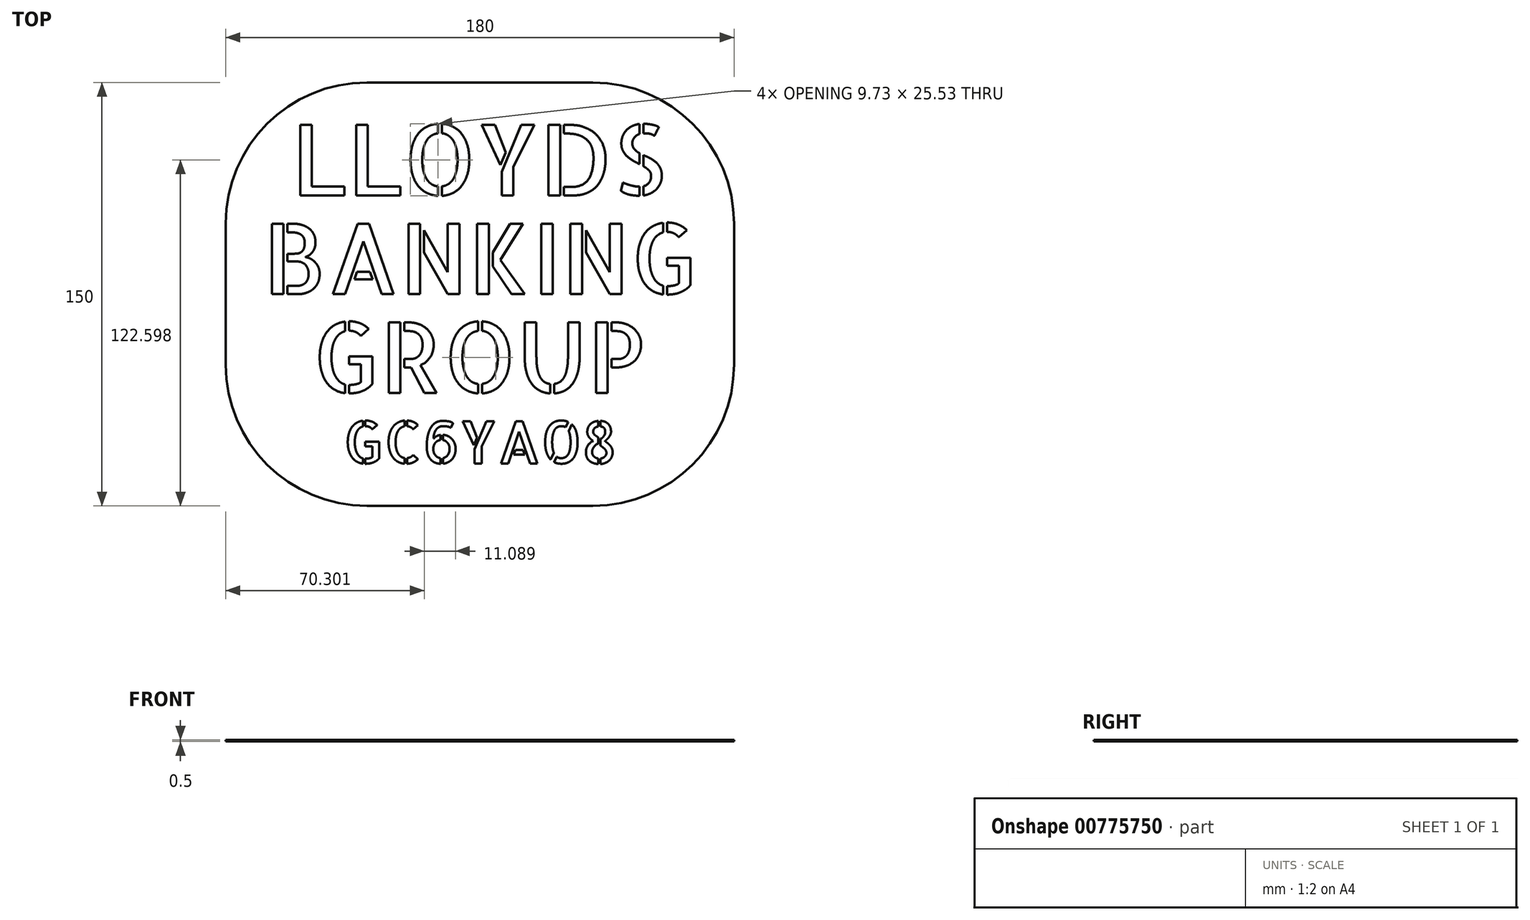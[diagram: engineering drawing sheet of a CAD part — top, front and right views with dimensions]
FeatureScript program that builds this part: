
annotation { "Feature Type Name" : "Feature", "Feature Type Description" : "" }
export const myFeature = defineFeature(function(context is Context, id is Id, definition is map)
    precondition{}
    {
        {
            var Q0;
            Q0=qCreatedBy(makeId("Top.planeOp"),FACE);
            var sketch = newSketch(context, id + "F0", { "sketchPlane" : qUnion([Q0])});
            skText(sketch, "E0", { "text": "LLOYDS", "fontName": "AllertaStencil-Regular.ttf"});
            skLineSegment(sketch, "E1.bottom", {"start": v(-105, 148.5) * mm, "end": v(105, 148.5) * mm, "construction": true});
            skLineSegment(sketch, "E1.top", {"start": v(-105, -148.5) * mm, "end": v(105, -148.5) * mm, "construction": true});
            skLineSegment(sketch, "E1.left", {"start": v(-105, 148.5) * mm, "end": v(-105, -148.5) * mm, "construction": true});
            skLineSegment(sketch, "E1.right", {"start": v(105, 148.5) * mm, "end": v(105, -148.5) * mm, "construction": true});
            skPoint(sketch, "E1.middle", {"position": v(0, 0) * mm});
            skText(sketch, "E2", { "text": "GC6YA08", "fontName": "AllertaStencil-Regular.ttf"});
            skLineSegment(sketch, "E3.bottom", {"start": v(90, 70) * mm, "end": v(-90, 70) * mm});
            skLineSegment(sketch, "E3.top", {"start": v(90, -80) * mm, "end": v(-90, -80) * mm});
            skLineSegment(sketch, "E3.left", {"start": v(90, 70) * mm, "end": v(90, -80) * mm});
            skLineSegment(sketch, "E3.right", {"start": v(-90, 70) * mm, "end": v(-90, -80) * mm});
            skPoint(sketch, "E3.middle", {"position": v(0, -5) * mm});
            skPoint(sketch, "E4", {"position": v(0, 70) * mm});
            skText(sketch, "E5", { "text": "BANKING", "fontName": "AllertaStencil-Regular.ttf"});
            skText(sketch, "E6", { "text": "GROUP", "fontName": "AllertaStencil-Regular.ttf"});
            const initialGuessF0  = {"E0": [-0.06678, 0.03, 1, 0, 0.025], "E2": [-0.0484, -0.065, 1, 0, 0.015], "E5": [-0.0769, -0.005, 1, 0, 0.025], "E6": [-0.0594, -0.04, 1, 0, 0.025]};
            skSetInitialGuess(sketch, initialGuessF0);
            skSolve(sketch);
        }
        {
            var Q0;
            Q0=makeQuery(id+"F0.imprint","IMPRINT",FACE,{"disambiguationData":[TD([[makeQuery(id+"F0.imprint","IMPRINT",EDGE,{"derivedFrom":sQuery(id+"F0.wireOp",EDGE,"E0.sketch_text.stroke-0")}),1.0]])]});
            extrude(context, id + "F1", {"entities" : qUnion([Q0]), "depth" : 0.5 * mm, "offsetDistance" : 25 * mm});
        }
        {
            var Q0;
            Q0=makeQuery(id+"F1.opExtrude","SWEPT_EDGE",EDGE,{"disambiguationData":[OSD([sQuery(id+"F0.wireOp",EDGE,"E3.bottom"),sQuery(id+"F0.wireOp",EDGE,"E3.right")])]});
            var Q1;
            Q1=makeQuery(id+"F1.opExtrude","SWEPT_EDGE",EDGE,{"disambiguationData":[OSD([sQuery(id+"F0.wireOp",EDGE,"E3.top"),sQuery(id+"F0.wireOp",EDGE,"E3.right")])]});
            var Q2;
            Q2=makeQuery(id+"F1.opExtrude","SWEPT_EDGE",EDGE,{"disambiguationData":[OSD([sQuery(id+"F0.wireOp",EDGE,"E3.top"),sQuery(id+"F0.wireOp",EDGE,"E3.left")])]});
            var Q3;
            Q3=makeQuery(id+"F1.opExtrude","SWEPT_EDGE",EDGE,{"disambiguationData":[OSD([sQuery(id+"F0.wireOp",EDGE,"E3.bottom"),sQuery(id+"F0.wireOp",EDGE,"E3.left")])]});
            fillet(context, id + "F2", {"entities" : qUnion([Q0, Q1, Q2, Q3]), "radius" : 50 * mm, "tangentPropagation" : true, "allowEdgeOverflow" : false});
        }
    });
